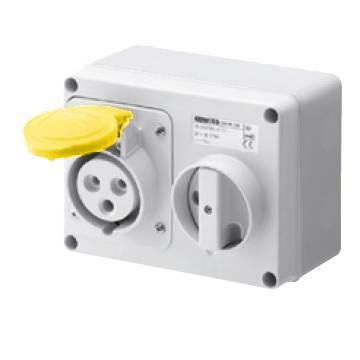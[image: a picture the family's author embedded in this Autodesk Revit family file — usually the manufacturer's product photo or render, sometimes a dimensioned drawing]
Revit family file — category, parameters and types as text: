
# Revit family: Building-IEC309Connections-GEWISS-44IB-INTERLOCKED-SOCKET-OUTLETS_IP44_WITH_BOTTOM
name_source: partatom
category: Apparecchi elettrici
revit_build: Autodesk Revit 2016 (Build: 20161004_0715(x64)
units: mm (PartAtom-declared; Revit-internal decimal feet)

## family parameters
Condiviso = No
Host = Muro
Mantenere orientamento annotazione = Sì
Numero OmniClass = 23.80.50.14
Punto di calcolo locali = No
Quota connettore circolare = Usa diametro
Sempre verticale = Sì
Taglio con vuoti quando caricato = No
Tipo di parte = Normale
Titolo OmniClass = Plug Connectors

## types (22) — shared parameters
Altezza da terra = 820 mm
Carico apparente = 0 VA
Catalogue = BUILDING
Catalogue Range = 44 IB
Classificazione carico = Altro
Electrocod = 2220
Frequency = 50/60 Hz
Glow Wire Test = 850 °C (active parts) - 650 °C (passive parts)
Glow wire test: = 850 °C (active parts) - 650 °C (passive parts)
IDF = e013b842-d6f1-4fba-800c-bd3a9423ad0b
IDT = 54ab296f-77ff-4020-be1a-67a03cbf098f
IP degree = IP44
Immagine tipo = GW66010.jpg
Numero poli = 3
Operating temperature: = -25 +40 °C
Potenza = 500 V
Presa = GEWISS - NERO
Produttore = GEWISS S.p.A.
Protection = NO (SBF)
Rated frequency (Hz) = 50/60 Hz
SEO = Socket outlet
Shock resistance = IK08
Struttura = GEWISS - Grigio RAL - 7035
Technical sheet = https://www.gewiss.com
Thermo-pressure with ball = 125 °C (active parts) - 80 °C (passive parts)
Tipo Simbolo = PRESAIND : 3P
Typology = Horizontal
URL = https://www.gewiss.com
Version file RFA = 18.0
Vetro = GEWISS - vetro
With back-mounting box = Yes
Working temperature = -25 ÷ +40 °C

## per-type parameters (varying)
| type | Colour | Colour: | Descrizione | EAN code | Modello | No. of poles | Number of poles | Rated current (A) | Rated current (In) | Rated voltage | Reference h |
| GW66013 - 32A 3P+E 110V H.INT.SOCK.O.W.B. 4H SBF | Yellow | Yellow | 32A 3P+E 110V H.INT.SOCK.O.W.B. 4H SBF | 8011564006164 | GW66013 | 3P+E | 3P+E | 32 | 32 | 100-130V | 4 |
| GW66014 - 32A 3P+N+E 110V H.INT.SOCK.O.W.B. 4H SBF | Yellow | Yellow | 32A 3P+N+E 110V H.INT.SOCK.O.W.B. 4H SBF | 8011564006195 | GW66014 | 3P+N+E | 3P+N+E | 32 | 32 | 100-130V | 4 |
| GW66017 - 32A 3P+N+E 230V H.INT.SOCK.O.W.B. 9H SBF | Blue | Blue | 32A 3P+N+E 230V H.INT.SOCK.O.W.B. 9H SBF | 8011564006201 | GW66017 | 3P+N+E | 3P+N+E | 32 | 32 | 200-250V | 9 |
| GW66005 - 16A 3P+E 230V H.INT.SOCK.O.W.B. 9H SBF | Blue | Blue | 16A 3P+E 230V H.INT.SOCK.O.W.B. 9H SBF | 8011564005815 | GW66005 | 3P+E | 3P+E | 16 | 16 | 200-250V | 9 |
| GW66015 - 32A 2P+E 230V H.INT.SOCK.O.W.B. 6H SBF | Blue | Blue | 32A 2P+E 230V H.INT.SOCK.O.W.B. 6H SBF | 8011564006102 | GW66015 | 2P+E | 2P+E | 32 | 32 | 200-250V | 6 |
| GW66003 - 16A 3P+N+E 110V H.INT.SOCK.O.W.B. 4H SBF | Yellow | Yellow | 16A 3P+N+E 110V H.INT.SOCK.O.W.B. 4H SBF | 8011564005877 | GW66003 | 3P+N+E | 3P+N+E | 16 | 16 | 100-130V | 4 |
| GW66018 - 32A 2P+E 400V H.INT.SOCK.O.W.B. 9H SBF | Red | Red | 32A 2P+E 400V H.INT.SOCK.O.W.B. 9H SBF | 8011564006157 | GW66018 | 2P+E | 2P+E | 32 | 32 | 380-415V | 9 |
| GW66006 - 16A 3P+N+E 230V H.INT.SOCK.O.W.B. 9H SBF | Blue | Blue | 16A 3P+N+E 230V H.INT.SOCK.O.W.B. 9H SBF | 8011564005884 | GW66006 | 3P+N+E | 3P+N+E | 16 | 16 | 200-250V | 9 |
| GW66001 - 16A 2P+E 110V H.INT.SOCK.O.W.B. 4H SBF | Yellow | Yellow | 16A 2P+E 110V H.INT.SOCK.O.W.B. 4H SBF | 8011564005792 | GW66001 | 2P+E | 2P+E | 16 | 16 | 100-130V | 4 |
| GW66016 - 32A 3P+E 230V H.INT.SOCK.O.W.B. 9H SBF | Blue | Blue | 32A 3P+E 230V H.INT.SOCK.O.W.B. 9H SBF | 8011564006171 | GW66016 | 3P+E | 3P+E | 32 | 32 | 200-250V | 9 |
| GW66004 - 16A 2P+E 230V H.INT.SOCK.O.W.B. 6H SBF | Blue | Blue | 16A 2P+E 230V H.INT.SOCK.O.W.B. 6H SBF | 8011564005808 | GW66004 | 2P+E | 2P+E | 16 | 16 | 200-250V | 6 |
| GW66019 - 32A 3P+E 400V H.INT.SOCK.O.W.B. 6H SBF | Red | Red | 32A 3P+E 400V H.INT.SOCK.O.W.B. 6H SBF | 8011564006126 | GW66019 | 3P+E | 3P+E | 32 | 32 | 380-415V | 6 |
| GW66008 - 16A 3P+E 400V H.INT.SOCK.O.W.B. 6H SBF | Red | Red | 16A 3P+E 400V H.INT.SOCK.O.W.B. 6H SBF | 8011564005822 | GW66008 | 3P+E | 3P+E | 16 | 16 | 380-415V | 6 |
| GW66022 - 32A 3P+N+E 500V H.INT.SOCK.O.W.B. 7H SBF | Black | Black | 32A 3P+N+E 500V H.INT.SOCK.O.W.B. 7H SBF | 8011564006218 | GW66022 | 3P+N+E | 3P+N+E | 32 | 32 | 480-500V | 7 |
| GW66011 - 16A 3P+N+E 500V H.INT.SOCK.O.W.B. 7H SBF | Black | Black | 16A 3P+N+E 500V H.INT.SOCK.O.W.B. 7H SBF | 8011564006096 | GW66011 | 3P+N+E | 3P+N+E | 16 | 16 | 480-500V | 7 |
| GW66020 - 32A 3P+N+E 400V H.INT.SOCK.O.W.B. 6H SBF | Red | Red | 32A 3P+N+E 400V H.INT.SOCK.O.W.B. 6H SBF | 8011564006133 | GW66020 | 3P+N+E | 3P+N+E | 32 | 32 | 380-415V | 6 |
| GW66009 - 16A 3P+N+E 400V H.INT.SOCK.O.W.B. 6H SBF | Red | Red | 16A 3P+N+E 400V H.INT.SOCK.O.W.B. 6H SBF | 8011564005839 | GW66009 | 3P+N+E | 3P+N+E | 16 | 16 | 380-415V | 6 |
| GW66012 - 32A 2P+E 110V H.INT.SOCK.O.W.B. 4H SBF | Yellow | Yellow | 32A 2P+E 110V H.INT.SOCK.O.W.B. 4H SBF | 8011564006140 | GW66012 | 2P+E | 2P+E | 32 | 32 | 100-130V | 4 |
| GW66021 - 32A 3P+E 500V H.INT.SOCK.O.W.B. 7H SBF | Black | Black | 32A 3P+E 500V H.INT.SOCK.O.W.B. 7H SBF | 8011564006188 | GW66021 | 3P+E | 3P+E | 32 | 32 | 480-500V | 7 |
| GW66007 - 16A 2P+E 400V H.INT.SOCK.O.W.B. 9H SBF | Red | Red | 16A 2P+E 400V H.INT.SOCK.O.W.B. 9H SBF | 8011564005846 | GW66007 | 2P+E | 2P+E | 16 | 16 | 380-415V | 9 |
| GW66002 - 16A 3P+E 110V H.INT.SOCK.O.W.B. 4H SBF | Yellow | Yellow | 16A 3P+E 110V H.INT.SOCK.O.W.B. 4H SBF | 8011564005853 | GW66002 | 3P+E | 3P+E | 16 | 16 | 100-130V | 4 |
| GW66010 - 16A 3P+E 500V H.INT.SOCK.O.W.B. 7H SBF | Black | Black | 16A 3P+E 500V H.INT.SOCK.O.W.B. 7H SBF | 8011564005860 | GW66010 | 3P+E | 3P+E | 16 | 16 | 480-500V | 7 |

## geometry (parser evidence)
native form markers: Sweep x2
no freeform markers — native parametric forms only
